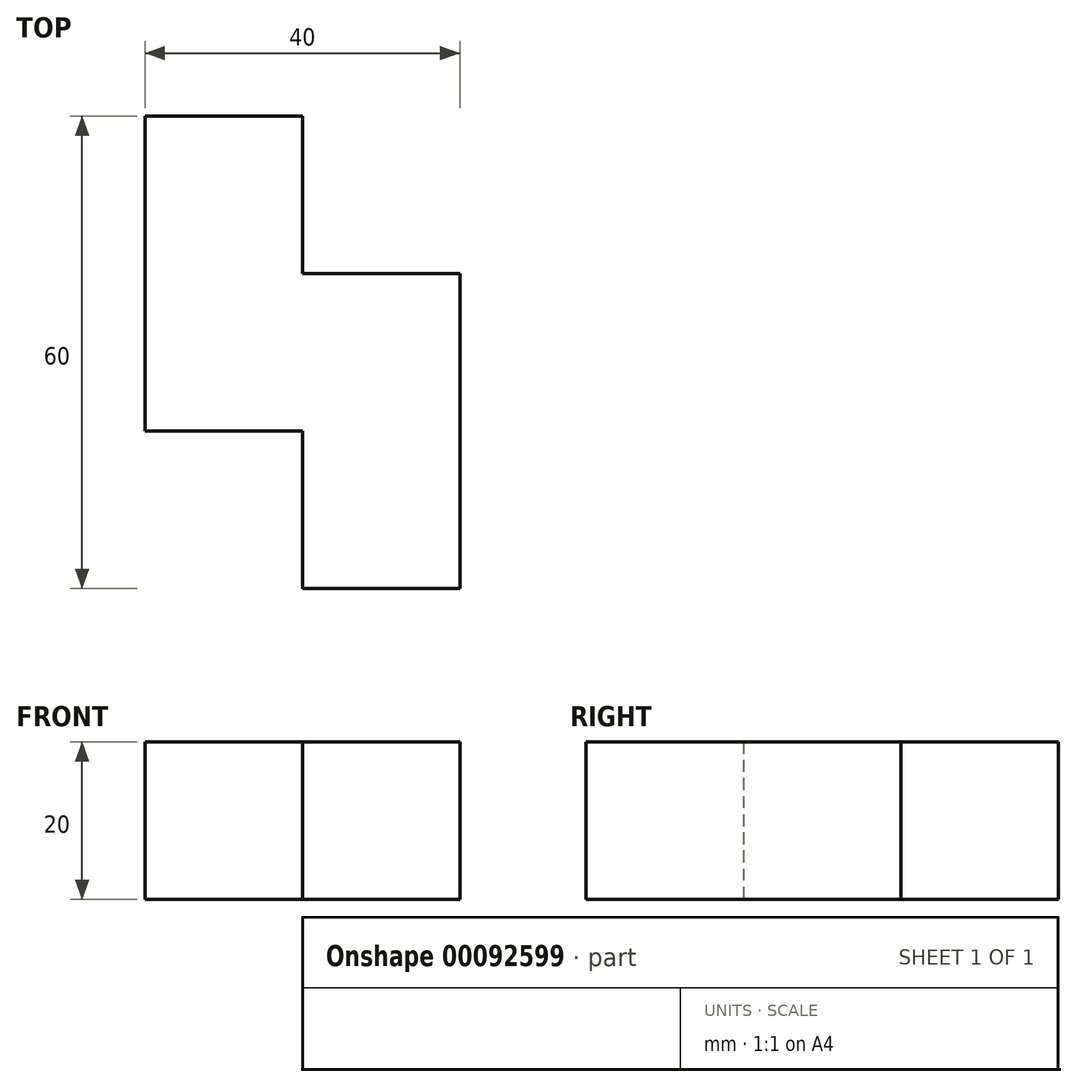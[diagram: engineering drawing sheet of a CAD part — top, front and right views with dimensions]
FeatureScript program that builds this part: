
annotation { "Feature Type Name" : "Feature", "Feature Type Description" : "" }
export const myFeature = defineFeature(function(context is Context, id is Id, definition is map)
    precondition{}
    {
        {
            var Q0;
            Q0=qCreatedBy(makeId("Top.planeOp"),FACE);
            var sketch = newSketch(context, id + "F0", { "sketchPlane" : qUnion([Q0])});
            skLineSegment(sketch, "E0.bottom", {"start": v(-40, 20) * mm, "end": v(-20, 20) * mm});
            skLineSegment(sketch, "E0.top", {"start": v(-40, -20) * mm, "end": v(-20, -20) * mm});
            skLineSegment(sketch, "E0.left", {"start": v(-40, 20) * mm, "end": v(-40, -20) * mm});
            skLineSegment(sketch, "E0.right", {"start": v(-20, 20) * mm, "end": v(-20, -20) * mm});
            skLineSegment(sketch, "E1.bottom", {"start": v(-20, 0) * mm, "end": v(0, 0) * mm});
            skLineSegment(sketch, "E1.top", {"start": v(-20, -40) * mm, "end": v(0, -40) * mm});
            skLineSegment(sketch, "E1.left", {"start": v(-20, 0) * mm, "end": v(-20, -40) * mm});
            skLineSegment(sketch, "E1.right", {"start": v(0, 0) * mm, "end": v(0, -40) * mm});
            skSolve(sketch);
        }
        {
            var Q0;
            Q0=makeQuery(id+"F0.imprint","IMPRINT",FACE,{"disambiguationData":[TD([[makeQuery(id+"F0.imprint","IMPRINT",EDGE,{"derivedFrom":sQuery(id+"F0.wireOp",EDGE,"E0.bottom")}),-1.0]])]});
            var Q1;
            {var subQ3=sQuery(id+"F0.wireOp",EDGE,"E1.bottom");Q1=makeQuery(id+"F0.imprint","IMPRINT",FACE,{"disambiguationData":[TD([[makeQuery(id+"F0.imprint","IMPRINT",EDGE,{"derivedFrom":subQ3}),-1.0]])]});}
            extrude(context, id + "F1", {"entities" : qUnion([Q0, Q1]), "depth" : 20 * mm});
        }
    });
